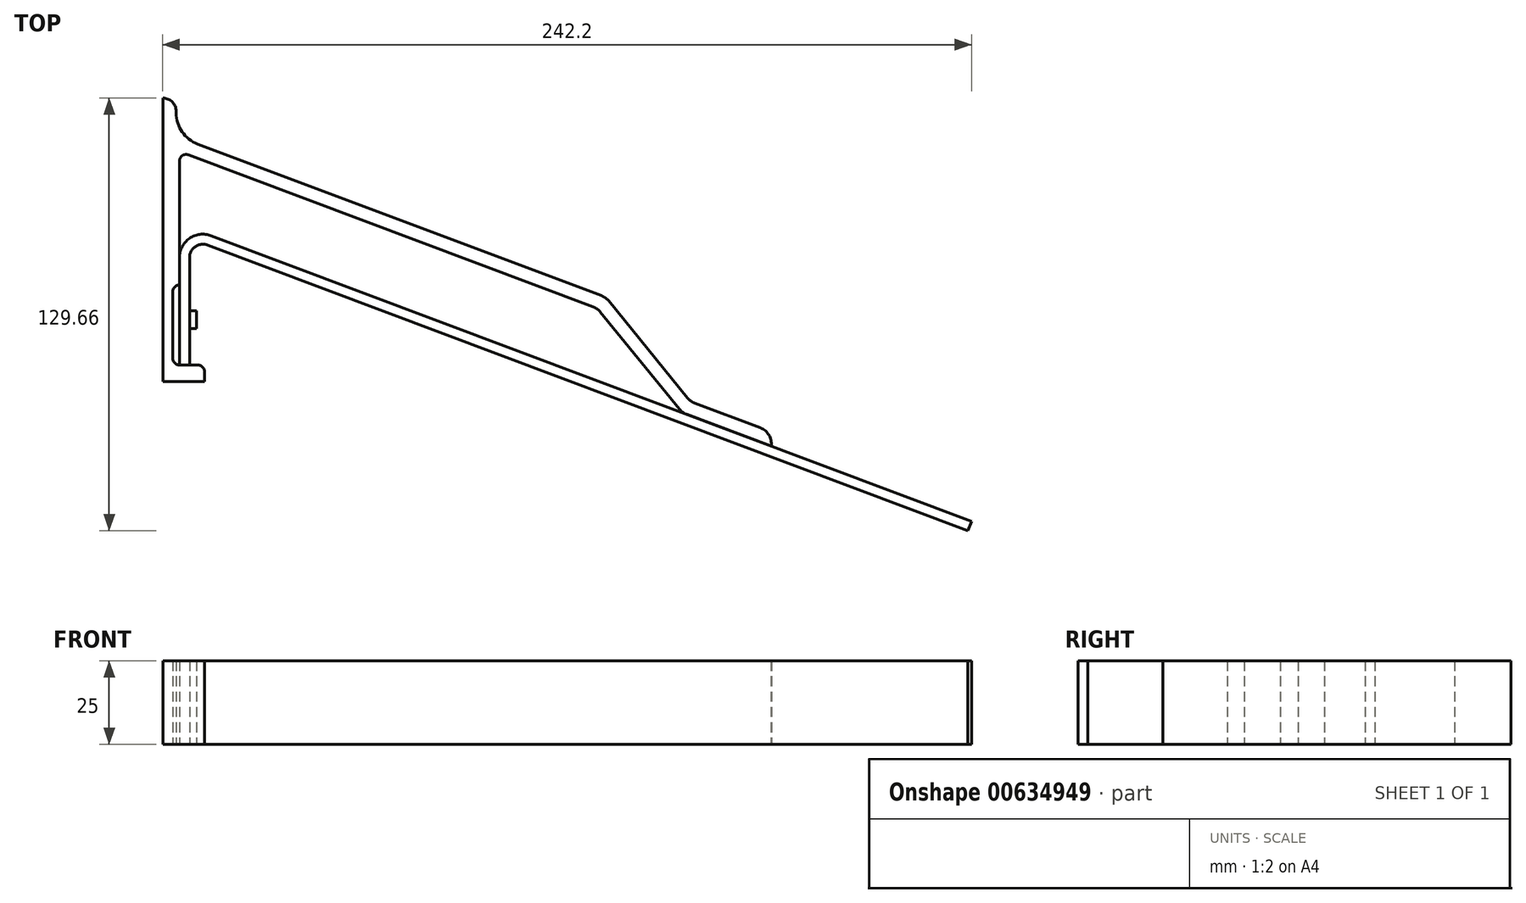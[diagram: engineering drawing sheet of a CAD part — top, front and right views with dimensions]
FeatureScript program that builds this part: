
annotation { "Feature Type Name" : "Feature", "Feature Type Description" : "" }
export const myFeature = defineFeature(function(context is Context, id is Id, definition is map)
    precondition{}
    {
        {
            var Q0;
            Q0=qCreatedBy(makeId("Top.planeOp"),FACE);
            var sketch = newSketch(context, id + "F0", { "sketchPlane" : qUnion([Q0])});
            skLineSegment(sketch, "E0", {"start": v(-28.4, -23.55) * mm, "end": v(-28.4, 61.45) * mm});
            skLineSegment(sketch, "E1", {"start": v(-28.4, -23.55) * mm, "end": v(-15.9, -23.55) * mm});
            skLineSegment(sketch, "E2", {"start": v(-15.9, -23.55) * mm, "end": v(-15.9, -20.55) * mm});
            skLineSegment(sketch, "E3", {"start": v(-17.9, -18.55) * mm, "end": v(-23.4, -18.55) * mm});
            skLineSegment(sketch, "E4", {"start": v(-25.4, -16.55) * mm, "end": v(-25.4, 3.45) * mm});
            skLineSegment(sketch, "E5", {"start": v(-23.4, 5.45) * mm, "end": v(-23.4, 5.45) * mm});
            skLineSegment(sketch, "E6", {"start": v(-23.4, 5.45) * mm, "end": v(-23.4, 42.56) * mm});
            skLineSegment(sketch, "E7", {"start": v(-20.7, 44.43) * mm, "end": v(100.54, -1.13) * mm});
            skLineSegment(sketch, "E8", {"start": v(102.66, -2.66) * mm, "end": v(126.34, -31.8) * mm});
            skLineSegment(sketch, "E9.0", {"start": v(-17.91, 47.66) * mm, "end": v(102.96, 2.23) * mm});
            skLineSegment(sketch, "E10", {"start": v(-28.4, 61.45) * mm, "end": v(-28.4, 57.45) * mm, "construction": true});
            skArc(sketch, "E11", {"start": v(-28.4, 61.45) * mm, "mid": v(-25.57, 60.28) * mm, "end": v(-24.4, 57.45) * mm});
            skLineSegment(sketch, "E12", {"start": v(-24.4, 57.45) * mm, "end": v(-24.4, 57.02) * mm});
            skArc(sketch, "E13", {"start": v(-24.4, 57.02) * mm, "mid": v(-22.62, 51.33) * mm, "end": v(-17.91, 47.66) * mm});
            skLineSegment(sketch, "E14.0", {"start": v(105.08, 0.7) * mm, "end": v(128.77, -28.44) * mm});
            skLineSegment(sketch, "E15", {"start": v(130.89, -29.96) * mm, "end": v(150.63, -37.38) * mm});
            skLineSegment(sketch, "E16.0", {"start": v(128.47, -33.33) * mm, "end": v(153.8, -42.85) * mm});
            skArc(sketch, "E17", {"start": v(150.63, -37.38) * mm, "mid": v(153.19, -39.55) * mm, "end": v(153.8, -42.85) * mm});
            skPoint(sketch, "E18.visualSharp", {"position": v(129.62, -29.49) * mm});
            skArc(sketch, "E18.filletArc", {"start": v(128.77, -28.44) * mm, "mid": v(129.72, -29.34) * mm, "end": v(130.89, -29.96) * mm});
            skPoint(sketch, "E19.visualSharp", {"position": v(127.2, -32.85) * mm});
            skArc(sketch, "E19.filletArc", {"start": v(126.34, -31.8) * mm, "mid": v(127.3, -32.7) * mm, "end": v(128.47, -33.33) * mm});
            skPoint(sketch, "E20.visualSharp", {"position": v(104.23, 1.75) * mm});
            skArc(sketch, "E20.filletArc", {"start": v(105.08, 0.7) * mm, "mid": v(104.13, 1.6) * mm, "end": v(102.96, 2.23) * mm});
            skPoint(sketch, "E21.visualSharp", {"position": v(101.8, -1.61) * mm});
            skArc(sketch, "E21.filletArc", {"start": v(102.66, -2.66) * mm, "mid": v(101.7, -1.76) * mm, "end": v(100.54, -1.13) * mm});
            skPoint(sketch, "E22.visualSharp", {"position": v(-23.4, 45.45) * mm});
            skArc(sketch, "E22.filletArc", {"start": v(-20.7, 44.43) * mm, "mid": v(-22.53, 44.2) * mm, "end": v(-23.4, 42.56) * mm});
            skPoint(sketch, "E23.visualSharp", {"position": v(-25.4, 5.45) * mm});
            skArc(sketch, "E23.filletArc", {"start": v(-23.4, 5.45) * mm, "mid": v(-24.81, 4.86) * mm, "end": v(-25.4, 3.45) * mm});
            skPoint(sketch, "E24.visualSharp", {"position": v(-25.4, -18.55) * mm});
            skArc(sketch, "E24.filletArc", {"start": v(-25.4, -16.55) * mm, "mid": v(-24.81, -17.97) * mm, "end": v(-23.4, -18.55) * mm});
            skPoint(sketch, "E25.visualSharp", {"position": v(-15.9, -18.55) * mm});
            skArc(sketch, "E25.filletArc", {"start": v(-15.9, -20.55) * mm, "mid": v(-16.48, -19.14) * mm, "end": v(-17.9, -18.55) * mm});
            skLineSegment(sketch, "E26", {"start": v(-1235.9, -134.84) * mm, "end": v(-1235.9, 112.84) * mm, "construction": true});
            skSolve(sketch);
        }
        {
            var Q0;
            Q0=qCreatedBy(makeId("Top.planeOp"),FACE);
            var sketch = newSketch(context, id + "F1", { "sketchPlane" : qUnion([Q0])});
            skLineSegment(sketch, "E27", {"start": v(-23.4, -18.55) * mm, "end": v(-23.4, 13.64) * mm});
            skLineSegment(sketch, "E28", {"start": v(-13.93, 20.2) * mm, "end": v(213.8, -65.4) * mm});
            skPoint(sketch, "E29.visualSharp", {"position": v(-23.4, 23.75) * mm});
            skArc(sketch, "E29.filletArc", {"start": v(-13.93, 20.2) * mm, "mid": v(-20.38, 19.4) * mm, "end": v(-23.4, 13.64) * mm});
            skLineSegment(sketch, "E30.0", {"start": v(-14.99, 17.39) * mm, "end": v(212.75, -68.21) * mm});
            skArc(sketch, "E30.1", {"start": v(-14.99, 17.39) * mm, "mid": v(-18.67, 16.93) * mm, "end": v(-20.4, 13.64) * mm});
            skLineSegment(sketch, "E30.2", {"start": v(-20.4, -18.55) * mm, "end": v(-20.4, 13.64) * mm});
            skLineSegment(sketch, "E31", {"start": v(212.75, -68.21) * mm, "end": v(213.8, -65.4) * mm});
            skLineSegment(sketch, "E32", {"start": v(-23.4, -18.55) * mm, "end": v(-20.4, -18.55) * mm});
            skSolve(sketch);
        }
        {
            var Q0;
            Q0=qCreatedBy(makeId("Top.planeOp"),FACE);
            var sketch = newSketch(context, id + "F2", { "sketchPlane" : qUnion([Q0])});
            skLineSegment(sketch, "E33.bottom", {"start": v(-20.4, -7.68) * mm, "end": v(-18.28, -7.68) * mm});
            skLineSegment(sketch, "E33.top", {"start": v(-20.4, -2.33) * mm, "end": v(-18.28, -2.33) * mm});
            skLineSegment(sketch, "E33.left", {"start": v(-20.4, -7.68) * mm, "end": v(-20.4, -2.33) * mm});
            skLineSegment(sketch, "E33.right", {"start": v(-18.28, -7.68) * mm, "end": v(-18.28, -2.33) * mm});
            skSolve(sketch);
        }
        {
            var Q0;
            Q0=makeQuery(id+"F0.imprint","IMPRINT",FACE,{"disambiguationData":[TD([[makeQuery(id+"F0.imprint","IMPRINT",EDGE,{"derivedFrom":sQuery(id+"F0.wireOp",EDGE,"E0")}),-1.0]])]});
            extrude(context, id + "F3", {"entities" : qUnion([Q0]), "depth" : 25 * mm, "offsetDistance" : 25 * mm});
        }
        {
            var Q0;
            Q0=makeQuery(id+"F1.imprint","IMPRINT",FACE,{"disambiguationData":[TD([[makeQuery(id+"F1.imprint","IMPRINT",EDGE,{"derivedFrom":sQuery(id+"F1.wireOp",EDGE,"E27")}),-1.0]])]});
            extrude(context, id + "F4", {"entities" : qUnion([Q0]), "depth" : 25 * mm, "offsetDistance" : 25 * mm});
        }
        {
            var Q0;
            Q0=makeQuery(id+"F2.imprint","IMPRINT",FACE,{"disambiguationData":[TD([[makeQuery(id+"F2.imprint","IMPRINT",EDGE,{"derivedFrom":sQuery(id+"F2.wireOp",EDGE,"E33.bottom")}),1.0]])]});
            extrude(context, id + "F5", {"entities" : qUnion([Q0]), "depth" : 25 * mm, "offsetDistance" : 25 * mm});
        }
    });
